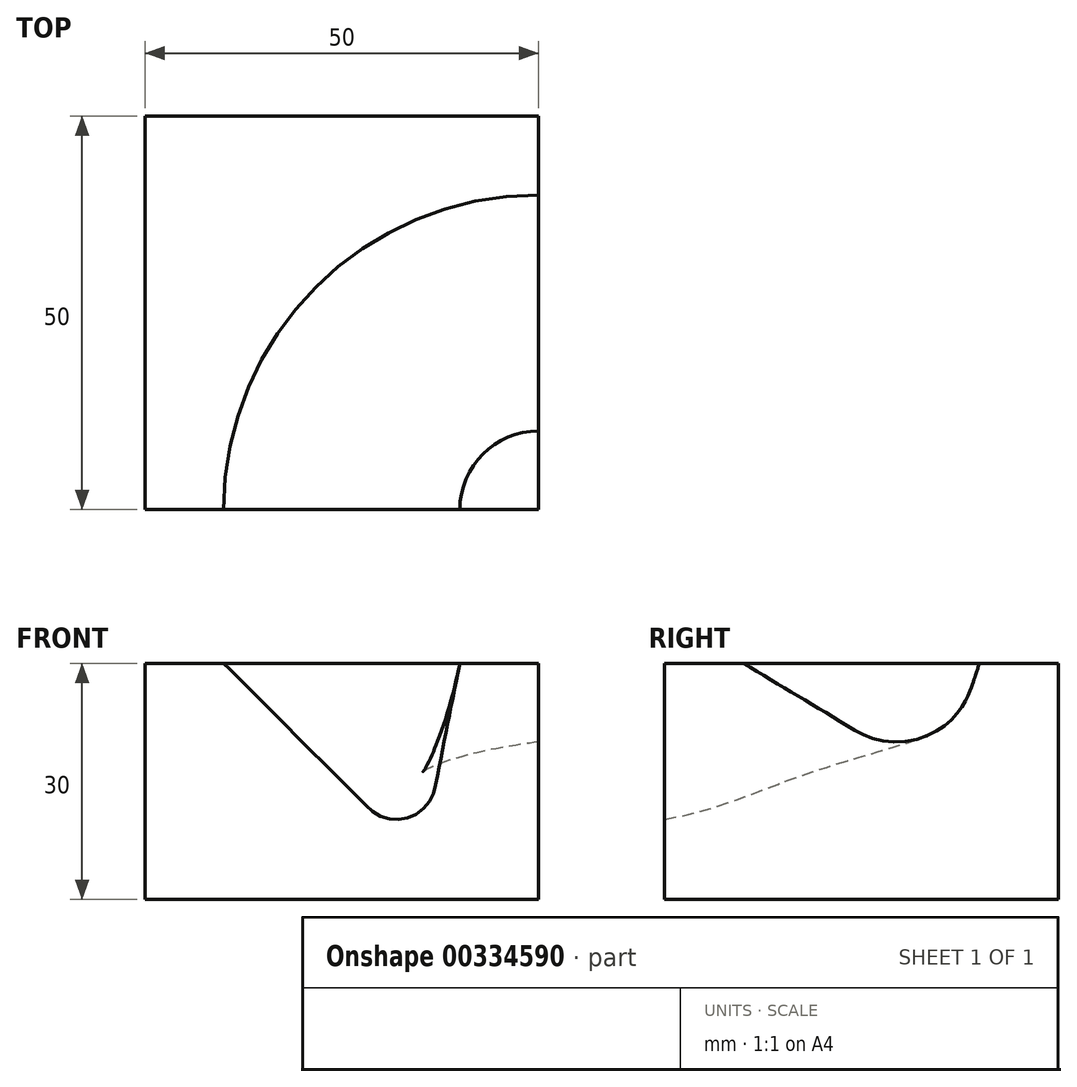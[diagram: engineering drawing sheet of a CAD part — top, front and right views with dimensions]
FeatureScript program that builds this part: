
annotation { "Feature Type Name" : "Feature", "Feature Type Description" : "" }
export const myFeature = defineFeature(function(context is Context, id is Id, definition is map)
    precondition{}
    {
        {
            var Q0;
            Q0=qCreatedBy(makeId("Top.planeOp"),FACE);
            var sketch = newSketch(context, id + "F0", { "sketchPlane" : qUnion([Q0])});
            skLineSegment(sketch, "E0.bottom", {"start": v(0, 0) * mm, "end": v(50, 0) * mm});
            skLineSegment(sketch, "E0.top", {"start": v(0, 50) * mm, "end": v(50, 50) * mm});
            skLineSegment(sketch, "E0.left", {"start": v(0, 0) * mm, "end": v(0, 50) * mm});
            skLineSegment(sketch, "E0.right", {"start": v(50, 0) * mm, "end": v(50, 50) * mm});
            skSolve(sketch);
        }
        {
            var Q0;
            Q0=makeQuery(id+"F0.imprint","IMPRINT",FACE,{"disambiguationData":[TD([[makeQuery(id+"F0.imprint","IMPRINT",EDGE,{"derivedFrom":sQuery(id+"F0.wireOp",EDGE,"E0.bottom")}),1.0]])]});
            extrude(context, id + "F1", {"entities" : qUnion([Q0]), "depth" : 30 * mm});
        }
        {
            var Q0;
            Q0=makeQuery(id+"F1.opExtrude","SWEPT_FACE",FACE,{"disambiguationData":[OSD([sQuery(id+"F0.wireOp",EDGE,"E0.bottom")])]});
            var sketch = newSketch(context, id + "F2", { "sketchPlane" : qUnion([Q0])});
            skLineSegment(sketch, "E1", {"start": v(10, 30) * mm, "end": v(28.4, 11.6) * mm});
            skLineSegment(sketch, "E2", {"start": v(36.83, 14.16) * mm, "end": v(40, 30) * mm});
            skPoint(sketch, "E3.visualSharp", {"position": v(35, 5) * mm});
            skArc(sketch, "E3.filletArc", {"start": v(28.4, 11.6) * mm, "mid": v(33.38, 10.36) * mm, "end": v(36.83, 14.16) * mm});
            skSolve(sketch);
        }
        {
            var Q0;
            Q0=makeQuery(id+"F1.opExtrude","SWEPT_FACE",FACE,{"disambiguationData":[OSD([sQuery(id+"F0.wireOp",EDGE,"E0.right")])]});
            var sketch = newSketch(context, id + "F3", { "sketchPlane" : qUnion([Q0])});
            skLineSegment(sketch, "E4", {"start": v(10, 30) * mm, "end": v(24.31, 21.41) * mm});
            skLineSegment(sketch, "E5", {"start": v(38.94, 26.83) * mm, "end": v(40, 30) * mm});
            skPoint(sketch, "E6.visualSharp", {"position": v(35, 15) * mm});
            skArc(sketch, "E6.filletArc", {"start": v(24.31, 21.41) * mm, "mid": v(32.92, 20.6) * mm, "end": v(38.94, 26.83) * mm});
            skSolve(sketch);
        }
        {
            var Q0;
            Q0=makeQuery(id+"F1.opExtrude","CAP_FACE",FACE,{"disambiguationData":[OSD([sQuery(id+"F0.wireOp",EDGE,"E0.bottom"),sQuery(id+"F0.wireOp",EDGE,"E0.top"),sQuery(id+"F0.wireOp",EDGE,"E0.left"),sQuery(id+"F0.wireOp",EDGE,"E0.right")])],"isStart":false});
            var sketch = newSketch(context, id + "F4", { "sketchPlane" : qUnion([Q0])});
            skCircle(sketch, "E7", {"center": v(50, 0) * mm, "radius": 10 * mm});
            skCircle(sketch, "E8", {"center": v(50, 0) * mm, "radius": 40 * mm});
            skSolve(sketch);
        }
        {
            var Q1;
            {var subQ0=sQuery(id+"F3.wireOp",EDGE,"E4");Q1=makeQuery(id+"F3.imprint","IMPRINT",FACE,{"disambiguationData":[TD([[makeQuery(id+"F3.imprint","IMPRINT",EDGE,{"derivedFrom":subQ0}),1.0]])]});}
            var Q2;
            {var subQ0=sQuery(id+"F2.wireOp",EDGE,"E1");Q2=makeQuery(id+"F2.imprint","IMPRINT",FACE,{"disambiguationData":[TD([[makeQuery(id+"F2.imprint","IMPRINT",EDGE,{"derivedFrom":subQ0}),1.0]])]});}
            var Q3;
            Q3=sQuery(id+"F4.wireOp",EDGE,"E8");
            var Q4;
            Q4=sQuery(id+"F4.wireOp",EDGE,"E7");
            loft(context, id + "F5", {"operationType" : NewBodyOperationType.REMOVE, "addGuides" : true, "sheetProfilesArray" : [{ "sheetProfileEntities" : qUnion([Q1]) }, { "sheetProfileEntities" : qUnion([Q2]) }], "guidesArray" : [{ "guideEntities" : qUnion([Q3]), "guideDerivativeType" : LoftGuideDerivativeType.DEFAULT, "guideDerivativeMagnitude" : 1 }, { "guideEntities" : qUnion([Q4]), "guideDerivativeType" : LoftGuideDerivativeType.DEFAULT, "guideDerivativeMagnitude" : 1 }]});
        }
    });
